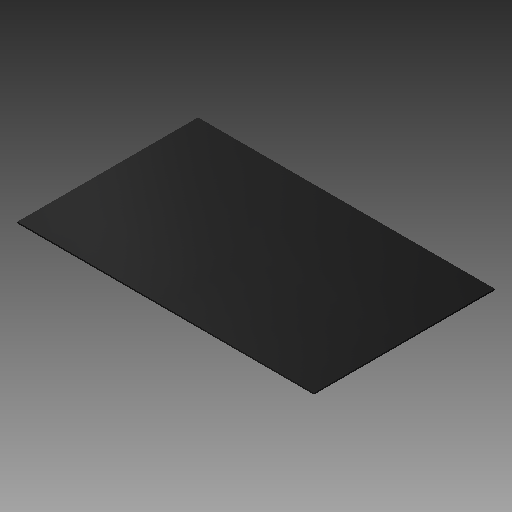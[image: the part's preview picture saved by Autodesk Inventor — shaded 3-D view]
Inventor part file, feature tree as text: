
AUTODESK INVENTOR PART (.ipt)
format: ipt  version: 2018 (Build 220112000, 112)  size: 99,840 bytes
history: native  units: mm
features: extrude x1
ambient origin geometry x8: Origin, YZ Plane, XZ Plane, XY Plane, X Axis, Y Axis, Z Axis, Center Point
bodies: Volumenkörper1 (feature_tree)
feature tree (1):
  extrude  "Extrusion1"  Depth=870.0mm
